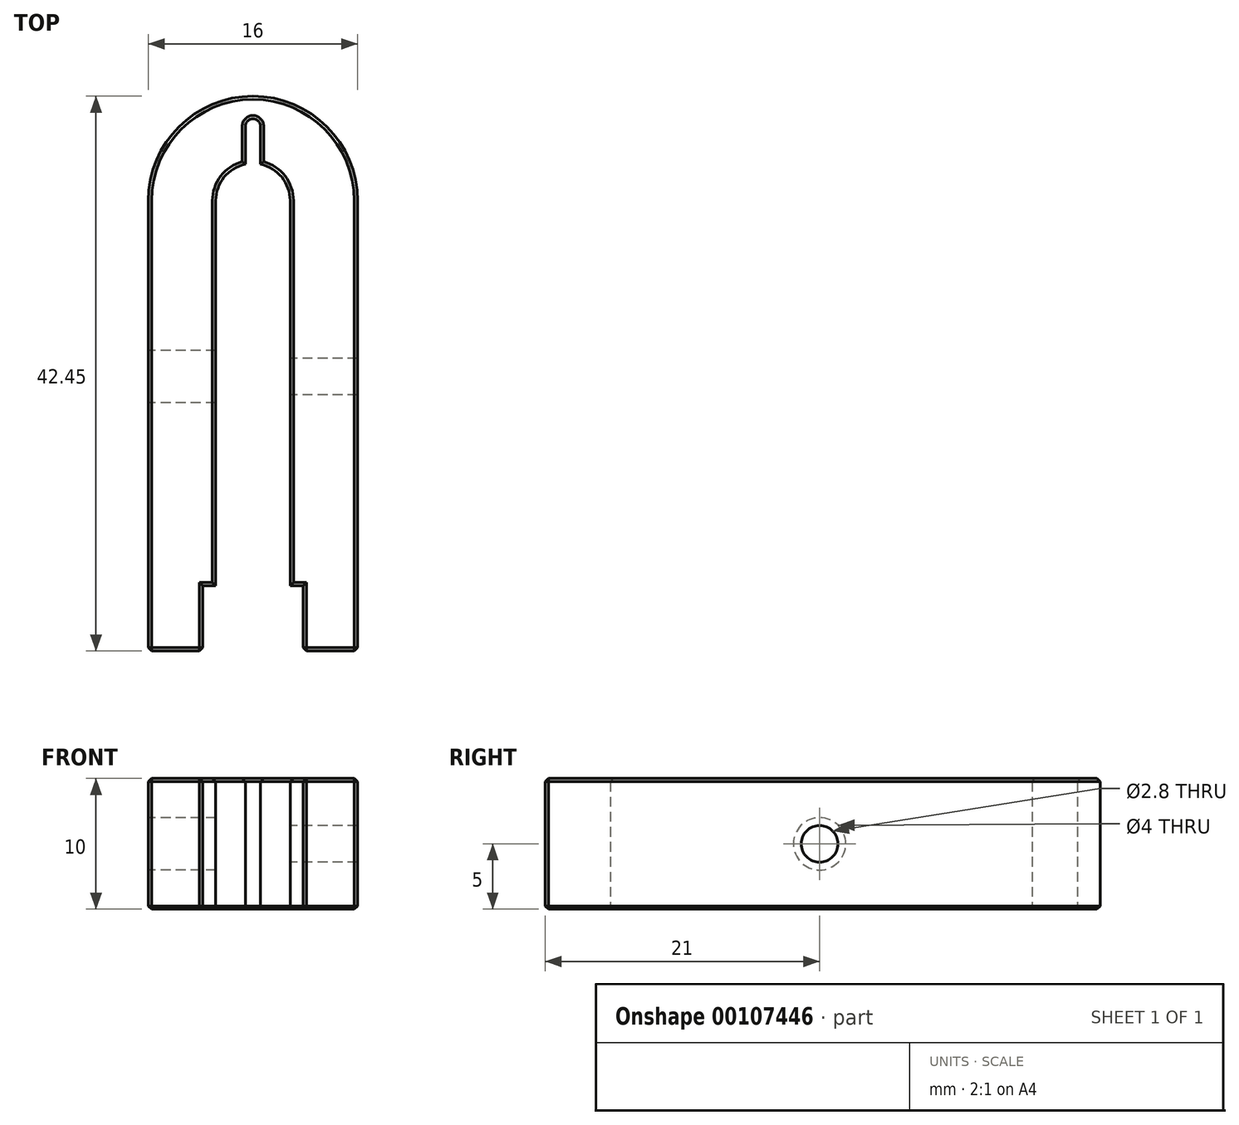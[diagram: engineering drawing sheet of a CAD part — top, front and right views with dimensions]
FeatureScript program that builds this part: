
annotation { "Feature Type Name" : "Feature", "Feature Type Description" : "" }
export const myFeature = defineFeature(function(context is Context, id is Id, definition is map)
    precondition{}
    {
        {
            var Q0;
            Q0=qCreatedBy(makeId("Top.planeOp"),FACE);
            var sketch = newSketch(context, id + "F0", { "sketchPlane" : qUnion([Q0])});
            skLineSegment(sketch, "E0.bottom", {"start": v(8, -20) * mm, "end": v(3.85, -20) * mm});
            skLineSegment(sketch, "E0.left", {"start": v(8, -20) * mm, "end": v(8, 14.45) * mm});
            skLineSegment(sketch, "E0.right", {"start": v(-8, -20) * mm, "end": v(-8, 14.45) * mm});
            skPoint(sketch, "E0.middle", {"position": v(0, 0) * mm});
            skLineSegment(sketch, "E1", {"start": v(-3.85, -20) * mm, "end": v(-3.85, -15) * mm});
            skLineSegment(sketch, "E2.MirrorCS", {"start": v(3.85, -20) * mm, "end": v(3.85, -15) * mm});
            skLineSegment(sketch, "E3.trimOffspring", {"start": v(-3.85, -20) * mm, "end": v(-8, -20) * mm});
            skArc(sketch, "E4", {"start": v(8, 14.45) * mm, "mid": v(0, 22.45) * mm, "end": v(-8, 14.45) * mm});
            skLineSegment(sketch, "E5", {"start": v(-3.85, -15) * mm, "end": v(-2.85, -15) * mm});
            skLineSegment(sketch, "E6.0", {"start": v(-2.85, -15) * mm, "end": v(-2.85, 14.45) * mm});
            skArc(sketch, "E6.1", {"start": v(2.85, 14.45) * mm, "mid": v(2.2, 16.25) * mm, "end": v(0.57, 17.24) * mm});
            skLineSegment(sketch, "E6.2", {"start": v(2.85, -15) * mm, "end": v(2.85, 14.45) * mm});
            skLineSegment(sketch, "E7.trimOffspring", {"start": v(2.85, -15) * mm, "end": v(3.85, -15) * mm});
            skLineSegment(sketch, "E8.left", {"start": v(0.57, 17.24) * mm, "end": v(0.57, 20.15) * mm});
            skLineSegment(sketch, "E8.right", {"start": v(-0.57, 17.24) * mm, "end": v(-0.57, 20.15) * mm});
            skArc(sketch, "E9", {"start": v(0.57, 20.15) * mm, "mid": v(0, 20.72) * mm, "end": v(-0.57, 20.15) * mm});
            skArc(sketch, "E10.trimOffspring", {"start": v(-0.57, 17.24) * mm, "mid": v(-2.2, 16.25) * mm, "end": v(-2.85, 14.45) * mm});
            skSolve(sketch);
        }
        {
            var Q0;
            Q0=makeQuery(id+"F0.imprint","IMPRINT",FACE,{"disambiguationData":[TD([[makeQuery(id+"F0.imprint","IMPRINT",EDGE,{"derivedFrom":sQuery(id+"F0.wireOp",EDGE,"E0.bottom")}),-1.0]])]});
            extrude(context, id + "F1", {"entities" : qUnion([Q0]), "depth" : 10 * mm});
        }
        {
            var Q0;
            Q0=makeQuery(id+"F1.opExtrude","SWEPT_FACE",FACE,{"disambiguationData":[OSD([sQuery(id+"F0.wireOp",EDGE,"E0.right")])]});
            var sketch = newSketch(context, id + "F2", { "sketchPlane" : qUnion([Q0])});
            skPoint(sketch, "E11", {"position": v(-1, 5) * mm});
            skPoint(sketch, "E11.positionSnap0", {"position": v(20, 5) * mm});
            skSolve(sketch);
        }
        {
            var Q0;
            Q0=sQuery(id+"F2.wireOp",VERTEX,"E11");
            var Q1;
            Q1=makeQuery(id+"F1.opExtrude","SWEPT_BODY",BODY,{"disambiguationData":[OSD([sQuery(id+"F0.wireOp",EDGE,"E0.bottom"),sQuery(id+"F0.wireOp",EDGE,"E0.left"),sQuery(id+"F0.wireOp",EDGE,"E0.right"),sQuery(id+"F0.wireOp",EDGE,"E1"),sQuery(id+"F0.wireOp",EDGE,"E2.MirrorCS"),sQuery(id+"F0.wireOp",EDGE,"E3.trimOffspring"),sQuery(id+"F0.wireOp",EDGE,"E4"),sQuery(id+"F0.wireOp",EDGE,"E5"),sQuery(id+"F0.wireOp",EDGE,"E6.0"),sQuery(id+"F0.wireOp",EDGE,"E6.1"),sQuery(id+"F0.wireOp",EDGE,"E6.2"),sQuery(id+"F0.wireOp",EDGE,"E7.trimOffspring"),sQuery(id+"F0.wireOp",EDGE,"E8.left"),sQuery(id+"F0.wireOp",EDGE,"E8.right"),sQuery(id+"F0.wireOp",EDGE,"E9"),sQuery(id+"F0.wireOp",EDGE,"E10.trimOffspring")])]});
            hole(context, id + "F3", {"style" : HoleStyle.C_BORE, "endStyle" : HoleEndStyle.THROUGH, "holeDiameter" : 2.8 * mm, "cBoreDiameter" : 4 * mm, "cBoreDepth" : 6 * mm, "startFromSketch" : true, "locations" : qUnion([Q0]), "scope" : qUnion([Q1]), "isTappedThrough" : true});
        }
        {
            var Q0;
            Q0=makeQuery(id+"F1.opExtrude","CAP_FACE",FACE,{"disambiguationData":[OSD([sQuery(id+"F0.wireOp",EDGE,"E0.bottom"),sQuery(id+"F0.wireOp",EDGE,"E0.left"),sQuery(id+"F0.wireOp",EDGE,"E0.right"),sQuery(id+"F0.wireOp",EDGE,"E1"),sQuery(id+"F0.wireOp",EDGE,"E2.MirrorCS"),sQuery(id+"F0.wireOp",EDGE,"E3.trimOffspring"),sQuery(id+"F0.wireOp",EDGE,"E4"),sQuery(id+"F0.wireOp",EDGE,"E5"),sQuery(id+"F0.wireOp",EDGE,"E6.0"),sQuery(id+"F0.wireOp",EDGE,"E6.1"),sQuery(id+"F0.wireOp",EDGE,"E6.2"),sQuery(id+"F0.wireOp",EDGE,"E7.trimOffspring"),sQuery(id+"F0.wireOp",EDGE,"E8.left"),sQuery(id+"F0.wireOp",EDGE,"E8.right"),sQuery(id+"F0.wireOp",EDGE,"E9"),sQuery(id+"F0.wireOp",EDGE,"E10.trimOffspring")])],"isStart":true});
            var Q1;
            Q1=makeQuery(id+"F1.opExtrude","CAP_FACE",FACE,{"disambiguationData":[OSD([sQuery(id+"F0.wireOp",EDGE,"E0.bottom"),sQuery(id+"F0.wireOp",EDGE,"E0.left"),sQuery(id+"F0.wireOp",EDGE,"E0.right"),sQuery(id+"F0.wireOp",EDGE,"E1"),sQuery(id+"F0.wireOp",EDGE,"E2.MirrorCS"),sQuery(id+"F0.wireOp",EDGE,"E3.trimOffspring"),sQuery(id+"F0.wireOp",EDGE,"E4"),sQuery(id+"F0.wireOp",EDGE,"E5"),sQuery(id+"F0.wireOp",EDGE,"E6.0"),sQuery(id+"F0.wireOp",EDGE,"E6.1"),sQuery(id+"F0.wireOp",EDGE,"E6.2"),sQuery(id+"F0.wireOp",EDGE,"E7.trimOffspring"),sQuery(id+"F0.wireOp",EDGE,"E8.left"),sQuery(id+"F0.wireOp",EDGE,"E8.right"),sQuery(id+"F0.wireOp",EDGE,"E9"),sQuery(id+"F0.wireOp",EDGE,"E10.trimOffspring")])],"isStart":false});
            var Q2;
            Q2=makeQuery(id+"F3.hole-0.boolean.opBoolean","COPY",FACE,{"derivedFrom":makeQuery(id+"F3.hole-0.opRevolve","SWEPT_FACE",FACE,{"disambiguationData":[OSD([sQuery(id+"F3.hole-0.sketch.wireOp",EDGE,"core_line_2")])]})});
            var Q3;
            Q3=makeQuery(id+"F3.hole-0.boolean.opBoolean","COPY",FACE,{"derivedFrom":makeQuery(id+"F3.hole-0.opRevolve","SWEPT_FACE",FACE,{"disambiguationData":[OSD([sQuery(id+"F3.hole-0.sketch.wireOp",EDGE,"cbore_start_line_2")])]})});
            var Q4;
            Q4=makeQuery(id+"F1.opExtrude","SWEPT_FACE",FACE,{"disambiguationData":[OSD([sQuery(id+"F0.wireOp",EDGE,"E3.trimOffspring")])]});
            var Q5;
            Q5=makeQuery(id+"F1.opExtrude","SWEPT_FACE",FACE,{"disambiguationData":[OSD([sQuery(id+"F0.wireOp",EDGE,"E0.bottom")])]});
            chamfer(context, id + "F4", {"entities" : qUnion([Q0, Q1, Q2, Q3, Q4, Q5]), "width" : .25 * mm, "tangentPropagation" : true});
        }
    });
